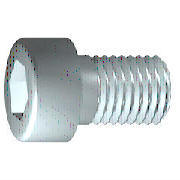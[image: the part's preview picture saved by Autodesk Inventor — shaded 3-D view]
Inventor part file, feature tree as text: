
AUTODESK INVENTOR PART (.ipt)
format: ipt  version: 2022 (Build 260153000, 153)  size: 198,656 bytes
history: native  units: mm (DEFAULTED — no unit token found)
features: sketch x2, extrude x1, plane x1, fillet x1
ambient origin geometry x7: Origin, YZ Plane, XY Plane, X Axis, Y Axis, Z Axis, Center Point
bodies: Solid1 (feature_tree), Body (feature_tree)
feature tree (5):
  extrude  "Slot"  Depth=3.0mm
  plane  "Work Plane1"
  fillet  "Fillet2"  Radius=3.0mm
  sketch  "Sketch1"  dims[d1=3.75mm d2=0.306825mm d3=3.0mm]
  sketch  "Sketch2"  dims[d4=1.3mm d5=60.0deg d6=3.0mm d7=3.0mm d8=2.886751mm d9=5.5mm d10=90.0deg d11=10.0mm d12=0.0mm d13=3.75mm d14=0.0mm d15=0.306725mm d16=0.306725mm d17=0.3mm d19=0.0mm d26=5.0mm d27=45.0deg d28=0.0mm d29=0.0mm d30=0.1mm]
